# Revit family: IS_ConnectAir_E0296_BIM_DE
name_source: partatom
category: Plumbing Fixtures
revit_build: Autodesk Revit MEP 2014 (Build: 20130308_1515(x64)
units: mm (PartAtom-declared; Revit-internal decimal feet)

## types (2) — shared parameters
Accessories = www.idealstandard.de\ersatzteile
AreaUnits = millimeters
Assembly Code = C1030200
AssetType = Fixed
Brand = Ideal Standard
CodePerformance = DIN EN 14688 CL 25, DIN EN 31
ConnectionType = Plumbing
Default Elevation = 850 mm  [stored 2.78871 ft]
DrainSize = 42 mm  [stored 0.137795 ft]
DurationUnit = year
ExpectedLife = 25
Features = Connect Air 54cm countertop washbasin, 1 taphole with overflow
GrossWeight = 0
IfcExportAs = IfcSanitaryType
IfcExportType = WASHHANDBASIN
InstallationInstructions = www.idealstandard.de\produkte
LinearUnits = millimeters
ManufacturerURL = www.idealstandard.de
Material = Vitreous china
NBSDescription = Counter top wash basins
NBSReference = 45-35-70/360
NettWeight = 13,5 kg
NominalHeight = 153 mm  [stored 0.501969 ft]
NominalLength = 381 mm
NominalWidth = 540 mm
ProductInformation = www.idealstandard.de\produkte
Shape = Sculptured
Size = 540x460x165mm
Space = Internal
URL = www.idealstandard.com
Uniclass2015Code = Pr_40_20_96_18
Uniclass2015Title = Counter top wash basins
Uniclass2015Version = Products v1.1
Version = 1
VolumeUnits = Litres
WarrantyDescription = Manufacturers Warranty
WarrantyDurationUnit = year
WashHandBasinMounting = i.e.Wall Hung
WashHandBasinType = Hand Rinse
zero-valued in all types: CWFU, Cost, HWFU, WFU

## per-type parameters (varying)
| type | BIMObjectName | BarCode | Color | Description | Finish | Model | ModelNumber | ModelReference | Name |
| E029601 - Connect Air 54cm countertop washbasin, 1 taphole with overflow | ISI_IdealStandard_CounterTopWashBasins_ConnectAir_E029601 | 5017830514411 | white | E029601 Connect Air 54cm countertop washbasin, 1 taphole with overflow | white | E029601 | E029601 | E029601 Connect Air 54cm countertop washbasin, 1 taphole with overflow | CounterTopWashBasins_ConnectAir_E029601_IdealStandard |
| E0296MA - Connect Air 54cm countertop washbasin, 1 taphole with overflow | ISI_IdealStandard_CounterTopWashBasins_ConnectAir_E0296MA | 5017830518389 | white with ideal plus | E0296MA Connect Air 54cm countertop washbasin, 1 taphole with overflow | white with ideal plus | E0296MA | E0296MA | E0296MA Connect Air 54cm countertop washbasin, 1 taphole with overflow | CounterTopWashBasins_ConnectAir_E0296MA_IdealStandard |

note: [stored X ft] marks values corroborated as IEEE doubles in the binary element streams (Revit-internal decimal feet)

## geometry (parser evidence)
native form markers: Sweep x2
no freeform markers — native parametric forms only
